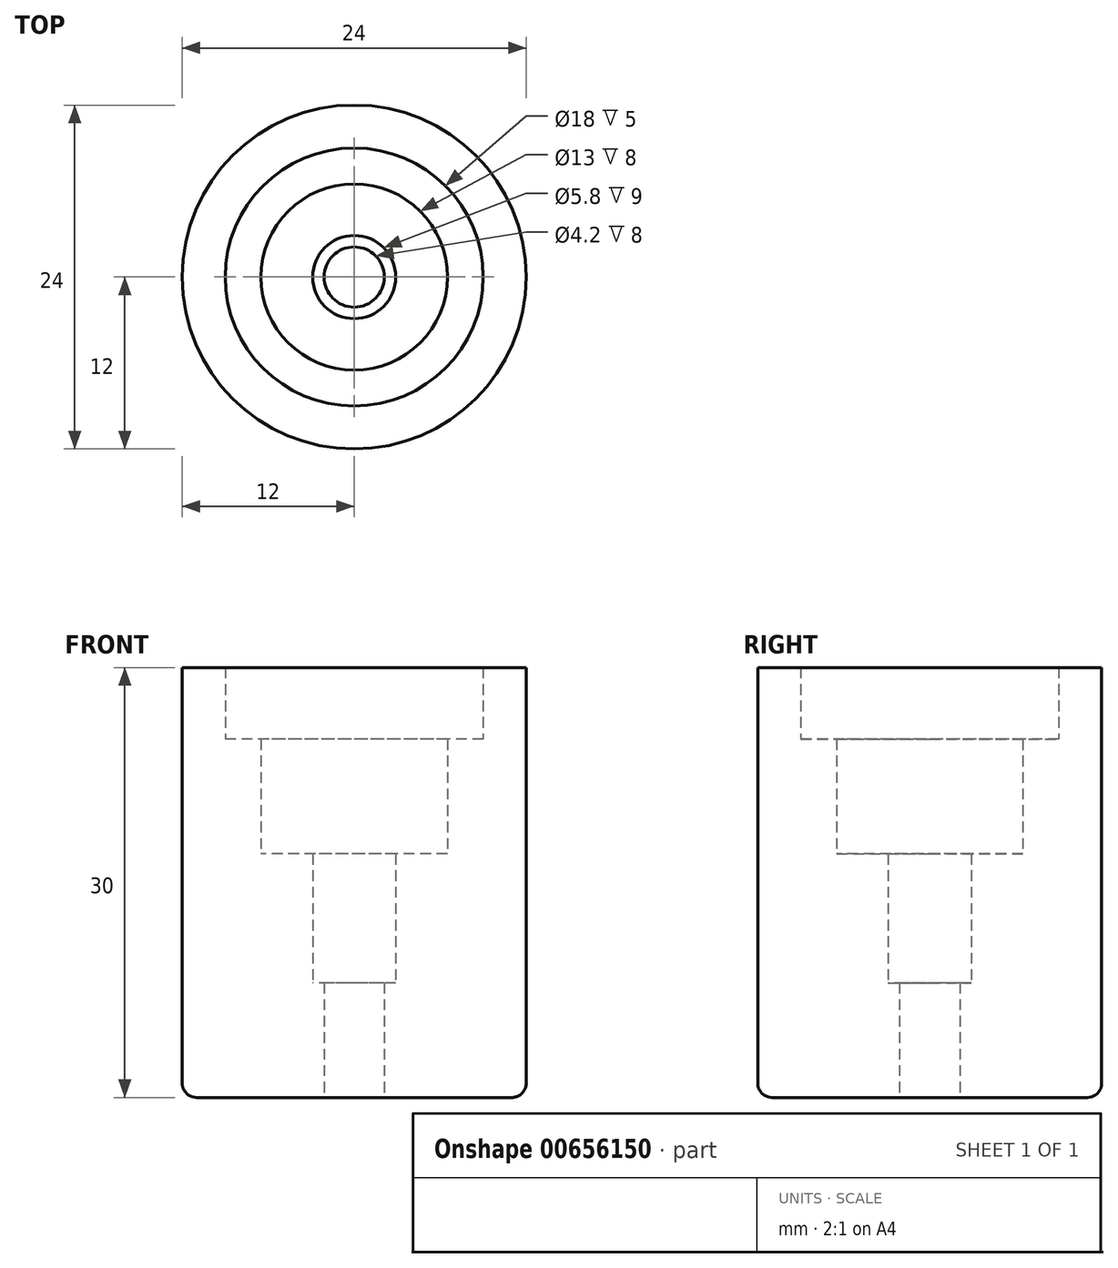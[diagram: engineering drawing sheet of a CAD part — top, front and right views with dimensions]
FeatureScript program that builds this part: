
annotation { "Feature Type Name" : "Feature", "Feature Type Description" : "" }
export const myFeature = defineFeature(function(context is Context, id is Id, definition is map)
    precondition{}
    {
        {
            var Q0;
            Q0=qCreatedBy(makeId("Top.planeOp"),FACE);
            var sketch = newSketch(context, id + "F0", { "sketchPlane" : qUnion([Q0])});
            skCircle(sketch, "E0", {"center": v(0, 0) * mm, "radius": 9 * mm});
            skCircle(sketch, "E1", {"center": v(0, 0) * mm, "radius": 12 * mm});
            skCircle(sketch, "E2", {"center": v(0, 0) * mm, "radius": 2.1 * mm});
            skCircle(sketch, "E3", {"center": v(0, 0) * mm, "radius": 2.9 * mm});
            skCircle(sketch, "E4", {"center": v(0, 0) * mm, "radius": 6.5 * mm});
            skSolve(sketch);
        }
        {
            var Q0;
            Q0=makeQuery(id+"F0.imprint","IMPRINT",FACE,{"disambiguationData":[TD([[makeQuery(id+"F0.imprint","IMPRINT",EDGE,{"derivedFrom":sQuery(id+"F0.wireOp",EDGE,"E0")}),-1.0]])]});
            extrude(context, id + "F1", {"entities" : qUnion([Q0]), "depth" : 30 * mm, "offsetDistance" : 25 * mm});
        }
        {
            var Q0;
            Q0=makeQuery(id+"F0.imprint","IMPRINT",FACE,{"disambiguationData":[TD([[makeQuery(id+"F0.imprint","IMPRINT",EDGE,{"derivedFrom":sQuery(id+"F0.wireOp",EDGE,"E0")}),1.0]])]});
            extrude(context, id + "F2", {"entities" : qUnion([Q0]), "operationType" : NewBodyOperationType.ADD, "depth" : 25 * mm, "offsetDistance" : 25 * mm});
        }
        {
            var Q0;
            Q0=makeQuery(id+"F0.imprint","IMPRINT",FACE,{"disambiguationData":[TD([[makeQuery(id+"F0.imprint","IMPRINT",EDGE,{"derivedFrom":sQuery(id+"F0.wireOp",EDGE,"E3")}),-1.0]])]});
            extrude(context, id + "F3", {"entities" : qUnion([Q0]), "operationType" : NewBodyOperationType.ADD, "depth" : 17 * mm, "offsetDistance" : 25 * mm});
        }
        {
            var Q0;
            Q0=makeQuery(id+"F0.imprint","IMPRINT",FACE,{"disambiguationData":[TD([[makeQuery(id+"F0.imprint","IMPRINT",EDGE,{"derivedFrom":sQuery(id+"F0.wireOp",EDGE,"E2")}),-1.0]])]});
            extrude(context, id + "F4", {"entities" : qUnion([Q0]), "operationType" : NewBodyOperationType.ADD, "depth" : 8 * mm, "offsetDistance" : 25 * mm});
        }
        {
            var Q0;
            Q0=makeQuery(id+"F1.opExtrude","CAP_EDGE",EDGE,{"disambiguationData":[OSD([sQuery(id+"F0.wireOp",EDGE,"E1")])],"isStart":true});
            fillet(context, id + "F5", {"entities" : qUnion([Q0]), "radius" : 1 * mm, "tangentPropagation" : true, "allowEdgeOverflow" : false});
        }
    });
